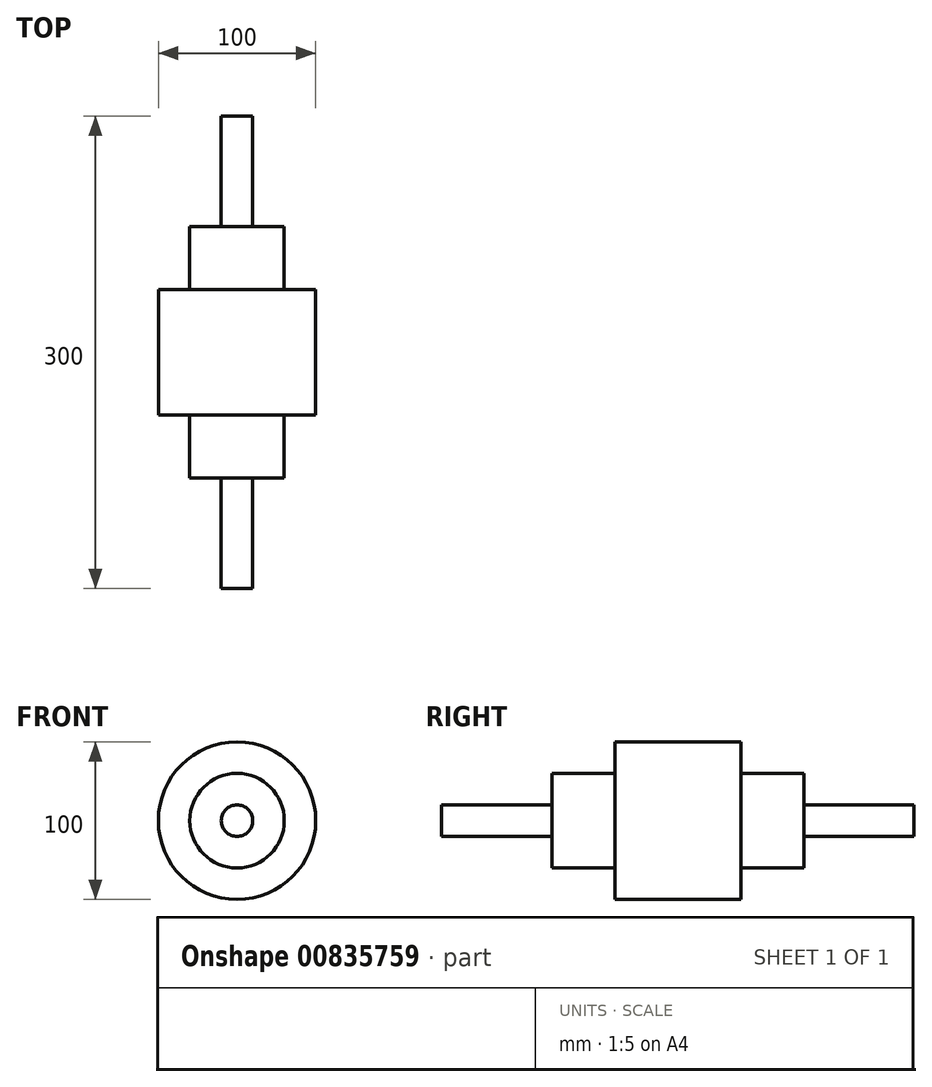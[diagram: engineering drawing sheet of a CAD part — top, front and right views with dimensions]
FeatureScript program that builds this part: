
annotation { "Feature Type Name" : "Feature", "Feature Type Description" : "" }
export const myFeature = defineFeature(function(context is Context, id is Id, definition is map)
    precondition{}
    {
        {
            var Q0;
            Q0=qCreatedBy(makeId("Front.planeOp"),FACE);
            var sketch = newSketch(context, id + "F0", { "sketchPlane" : qUnion([Q0])});
            skCircle(sketch, "E0", {"center": v(0, 0) * mm, "radius": 10 * mm});
            skCircle(sketch, "E1", {"center": v(0, 0) * mm, "radius": 30 * mm});
            skCircle(sketch, "E2", {"center": v(0, 0) * mm, "radius": 50 * mm});
            skSolve(sketch);
        }
        {
            var Q0;
            Q0=makeQuery(id+"F0.imprint","IMPRINT",FACE,{"disambiguationData":[TD([[makeQuery(id+"F0.imprint","IMPRINT",EDGE,{"derivedFrom":sQuery(id+"F0.wireOp",EDGE,"E0")}),1.0]])]});
            extrude(context, id + "F1", {"entities" : qUnion([Q0]), "depth" : 150 * mm, "offsetDistance" : 25 * mm});
        }
        {
            var Q0;
            Q0=makeQuery(id+"F0.imprint","IMPRINT",FACE,{"disambiguationData":[TD([[makeQuery(id+"F0.imprint","IMPRINT",EDGE,{"derivedFrom":sQuery(id+"F0.wireOp",EDGE,"E0")}),-1.0]])]});
            extrude(context, id + "F2", {"entities" : qUnion([Q0]), "operationType" : NewBodyOperationType.ADD, "depth" : 80 * mm, "offsetDistance" : 25 * mm});
        }
        {
            var Q0;
            Q0=makeQuery(id+"F0.imprint","IMPRINT",FACE,{"disambiguationData":[TD([[makeQuery(id+"F0.imprint","IMPRINT",EDGE,{"derivedFrom":sQuery(id+"F0.wireOp",EDGE,"E1")}),-1.0]])]});
            extrude(context, id + "F3", {"entities" : qUnion([Q0]), "operationType" : NewBodyOperationType.ADD, "depth" : 40 * mm, "offsetDistance" : 25 * mm});
        }
        {
            var Q0;
            Q0=makeQuery(id+"F1.opExtrude","SWEPT_BODY",BODY,{"disambiguationData":[OSD([sQuery(id+"F0.wireOp",EDGE,"E0")])]});
            var Q1;
            Q1=qCreatedBy(makeId("Front.planeOp"),FACE);
            mirror(context, id + "F4", {"operationType" : NewBodyOperationType.ADD, "entities" : qUnion([Q0]), "mirrorPlane" : qUnion([Q1])});
        }
    });
